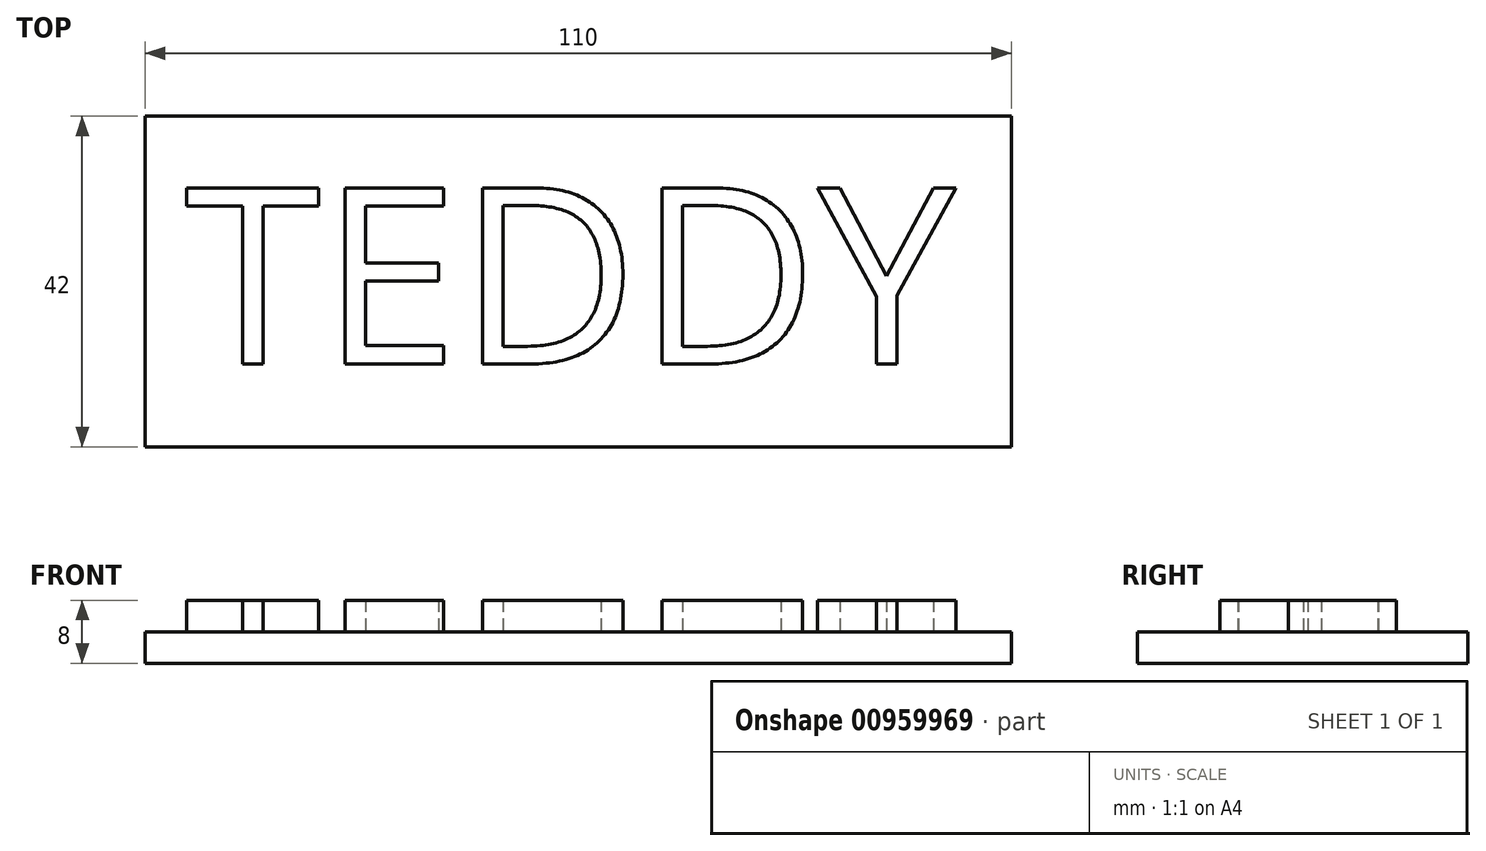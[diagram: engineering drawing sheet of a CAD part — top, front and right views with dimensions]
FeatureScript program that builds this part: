
annotation { "Feature Type Name" : "Feature", "Feature Type Description" : "" }
export const myFeature = defineFeature(function(context is Context, id is Id, definition is map)
    precondition{}
    {
        {
            var Q0;
            Q0=qCreatedBy(makeId("Top.planeOp"),FACE);
            var sketch = newSketch(context, id + "F0", { "sketchPlane" : qUnion([Q0])});
            skLineSegment(sketch, "E0.bottom", {"start": v(55, 21) * mm, "end": v(-55, 21) * mm});
            skLineSegment(sketch, "E0.top", {"start": v(55, -21) * mm, "end": v(-55, -21) * mm});
            skLineSegment(sketch, "E0.left", {"start": v(55, 21) * mm, "end": v(55, -21) * mm});
            skLineSegment(sketch, "E0.right", {"start": v(-55, 21) * mm, "end": v(-55, -21) * mm});
            skPoint(sketch, "E0.middle", {"position": v(0, 0) * mm});
            skSolve(sketch);
        }
        {
            var Q0;
            Q0=makeQuery(id+"F0.imprint","IMPRINT",FACE,{"disambiguationData":[TD([[makeQuery(id+"F0.imprint","IMPRINT",EDGE,{"derivedFrom":sQuery(id+"F0.wireOp",EDGE,"E0.bottom")}),1.0]])]});
            extrude(context, id + "F1", {"entities" : qUnion([Q0]), "depth" : 4 * mm, "offsetDistance" : 25 * mm});
        }
        {
            var Q0;
            Q0=makeQuery(id+"F1.opExtrude","CAP_FACE",FACE,{"disambiguationData":[OSD([sQuery(id+"F0.wireOp",EDGE,"E0.bottom"),sQuery(id+"F0.wireOp",EDGE,"E0.top"),sQuery(id+"F0.wireOp",EDGE,"E0.left"),sQuery(id+"F0.wireOp",EDGE,"E0.right")])],"isStart":false});
            var sketch = newSketch(context, id + "F2", { "sketchPlane" : qUnion([Q0])});
            skText(sketch, "E1", { "text": "TEDDY", "fontName": "OpenSans-Regular.ttf"});
            const initialGuessF2  = {"E1": [-0.05, -0.01047, 1, 0, 0.02255]};
            skSetInitialGuess(sketch, initialGuessF2);
            skSolve(sketch);
        }
        {
            var Q0;
            Q0=qSketchRegion(id+"F2",true);
            extrude(context, id + "F3", {"entities" : qUnion([Q0]), "operationType" : NewBodyOperationType.ADD, "depth" : 4 * mm, "offsetDistance" : 25 * mm});
        }
    });
